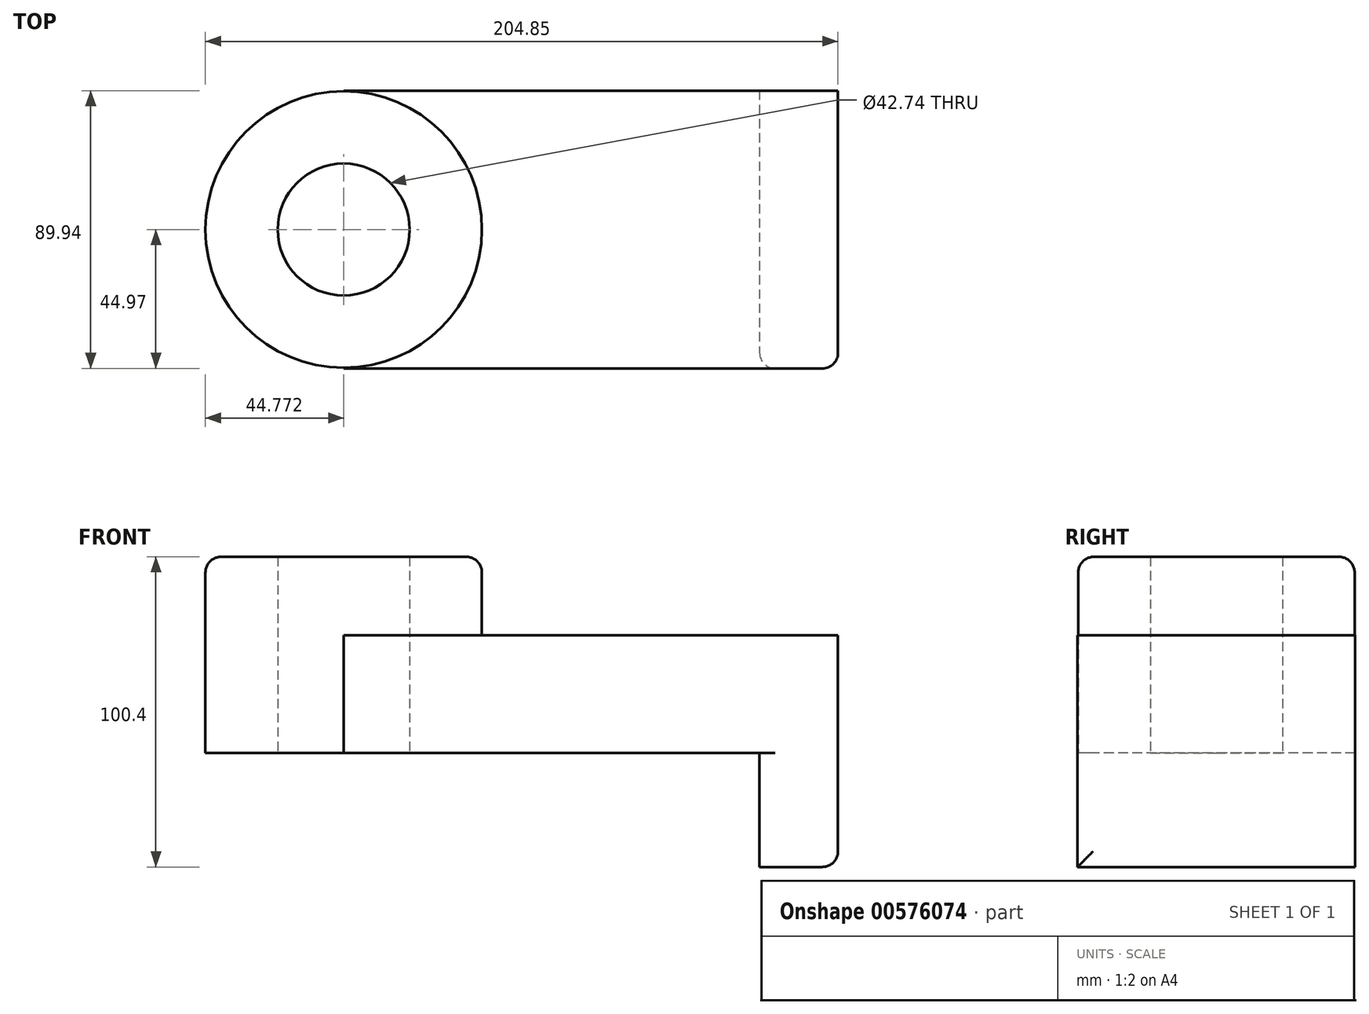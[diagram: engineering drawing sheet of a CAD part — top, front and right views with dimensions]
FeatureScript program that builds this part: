
annotation { "Feature Type Name" : "Feature", "Feature Type Description" : "" }
export const myFeature = defineFeature(function(context is Context, id is Id, definition is map)
    precondition{}
    {
        {
            var Q0;
            Q0=qCreatedBy(makeId("Top.planeOp"),FACE);
            var sketch = newSketch(context, id + "F0", { "sketchPlane" : qUnion([Q0])});
            skLineSegment(sketch, "E0.bottom", {"start": v(-67.34, 44.97) * mm, "end": v(67.34, 44.97) * mm});
            skLineSegment(sketch, "E0.top", {"start": v(-67.34, -44.97) * mm, "end": v(67.34, -44.97) * mm});
            skLineSegment(sketch, "E0.left", {"start": v(-67.34, 44.97) * mm, "end": v(-67.34, -44.97) * mm});
            skLineSegment(sketch, "E0.right", {"start": v(67.34, 44.97) * mm, "end": v(67.34, -44.97) * mm});
            skPoint(sketch, "E0.middle", {"position": v(0, 0) * mm});
            skCircle(sketch, "E1", {"center": v(-67.34, 0) * mm, "radius": 44.77 * mm});
            skCircle(sketch, "E2", {"center": v(-67.34, 0) * mm, "radius": 21.37 * mm});
            skSolve(sketch);
        }
        {
            var Q0;
            {var subQ1=sQuery(id+"F0.wireOp",EDGE,"E0.bottom");Q0=makeQuery(id+"F0.imprint","IMPRINT",FACE,{"disambiguationData":[TD([[makeQuery(id+"F0.imprint","IMPRINT",EDGE,{"derivedFrom":subQ1}),-1.0]])]});}
            extrude(context, id + "F1", {"entities" : qUnion([Q0]), "depth" : 38.1 * mm, "offsetDistance" : 25.4 * mm});
        }
        {
            var Q0;
            {var subQ0=sQuery(id+"F0.wireOp",EDGE,"E1");var subQ1=sQuery(id+"F0.wireOp",EDGE,"E0.left");var subQ2=makeQuery(id+"F0.imprint","INTERSECT",VERTEX,{"disambiguationData":[OD(0.0)],"derivedFrom":[subQ1,subQ0]});Q0=makeQuery(id+"F0.imprint","IMPRINT",FACE,{"disambiguationData":[TD([[makeQuery(id+"F0.imprint","IMPRINT",EDGE,{"disambiguationData":[TD([[subQ2,-1.0]])],"derivedFrom":subQ1}),-1.0]])]});}
            var Q1;
            {var subQ0=sQuery(id+"F0.wireOp",EDGE,"E1");var subQ1=sQuery(id+"F0.wireOp",EDGE,"E0.left");var subQ2=makeQuery(id+"F0.imprint","INTERSECT",VERTEX,{"disambiguationData":[OD(0.0)],"derivedFrom":[subQ1,subQ0]});Q1=makeQuery(id+"F0.imprint","IMPRINT",FACE,{"disambiguationData":[TD([[makeQuery(id+"F0.imprint","IMPRINT",EDGE,{"disambiguationData":[TD([[subQ2,-1.0]])],"derivedFrom":subQ1}),1.0]])]});}
            extrude(context, id + "F2", {"entities" : qUnion([Q0, Q1]), "operationType" : NewBodyOperationType.ADD, "depth" : 63.5 * mm, "offsetDistance" : 25.4 * mm});
        }
        {
            var Q0;
            Q0=makeQuery(id+"F2.opExtrude","CAP_EDGE",EDGE,{"disambiguationData":[OSD([sQuery(id+"F0.wireOp",EDGE,"E1")])],"isStart":false});
            fillet(context, id + "F3", {"entities" : qUnion([Q0]), "radius" : 5.08 * mm, "tangentPropagation" : true, "allowEdgeOverflow" : false});
        }
        {
            var Q0;
            Q0=makeQuery(id+"F1.opExtrude","SWEPT_FACE",FACE,{"disambiguationData":[OSD([sQuery(id+"F0.wireOp",EDGE,"E0.right")])]});
            var sketch = newSketch(context, id + "F4", { "sketchPlane" : qUnion([Q0])});
            skLineSegment(sketch, "E3.bottom", {"start": v(-44.97, 38.1) * mm, "end": v(44.97, 38.1) * mm});
            skLineSegment(sketch, "E3.top", {"start": v(-44.97, -36.9) * mm, "end": v(44.97, -36.9) * mm});
            skLineSegment(sketch, "E3.left", {"start": v(-44.97, 38.1) * mm, "end": v(-44.97, -36.9) * mm});
            skLineSegment(sketch, "E3.right", {"start": v(44.97, 38.1) * mm, "end": v(44.97, -36.9) * mm});
            skSolve(sketch);
        }
        {
            var Q0;
            Q0 = qSketchRegion(id + "F4", true);
            extrude(context, id + "F5", {"entities" : qUnion([Q0]), "operationType" : NewBodyOperationType.ADD, "depth" : 25.4 * mm, "offsetDistance" : 25.4 * mm});
        }
        {
            var Q0;
            Q0=makeQuery(id+"F5.opExtrude","CAP_EDGE",EDGE,{"disambiguationData":[OSD([sQuery(id+"F4.wireOp",EDGE,"E3.left")])],"isStart":false});
            var Q1;
            Q1=makeQuery(id+"F5.opExtrude","CAP_EDGE",EDGE,{"disambiguationData":[OSD([sQuery(id+"F4.wireOp",EDGE,"E3.left")])],"isStart":true});
            var Q2;
            Q2=makeQuery(id+"F5.opExtrude","CAP_EDGE",EDGE,{"disambiguationData":[OSD([sQuery(id+"F4.wireOp",EDGE,"E3.top")])],"isStart":false});
            fillet(context, id + "F6", {"entities" : qUnion([Q0, Q1, Q2]), "radius" : 5.08 * mm, "tangentPropagation" : true, "allowEdgeOverflow" : false});
        }
    });
